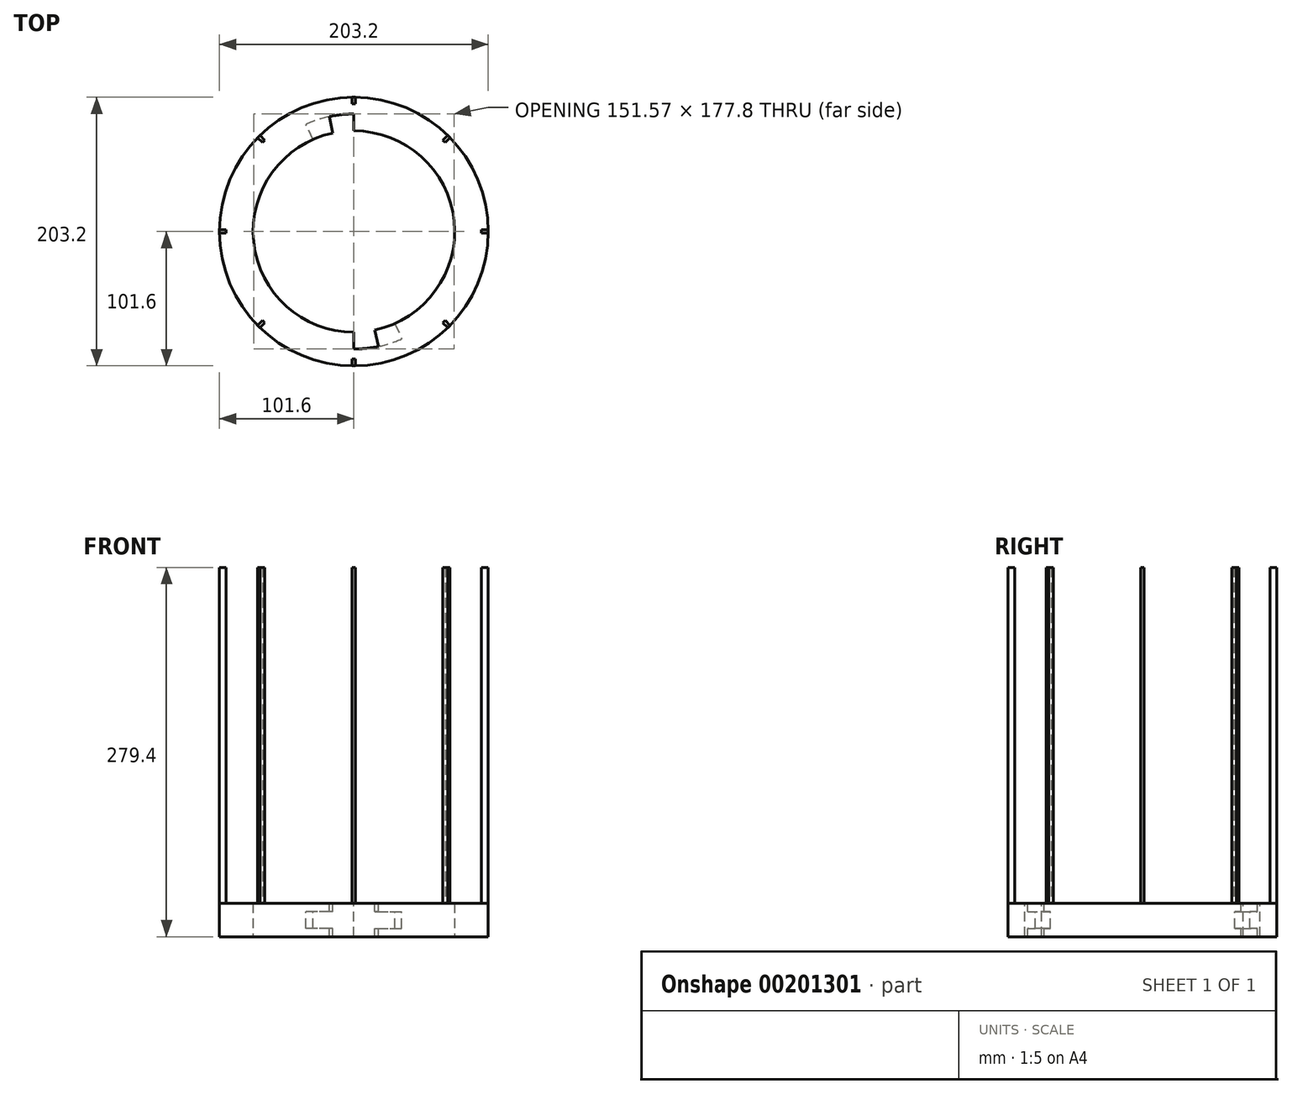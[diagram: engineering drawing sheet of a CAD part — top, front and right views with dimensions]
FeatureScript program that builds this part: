
annotation { "Feature Type Name" : "Feature", "Feature Type Description" : "" }
export const myFeature = defineFeature(function(context is Context, id is Id, definition is map)
    precondition{}
    {
        {
            var Q0;
            Q0=qCreatedBy(makeId("Top.planeOp"),FACE);
            var sketch = newSketch(context, id + "F0", { "sketchPlane" : qUnion([Q0])});
            skCircle(sketch, "E0", {"center": v(0, 0) * mm, "radius": 101.6 * mm});
            skCircle(sketch, "E1", {"center": v(0, 0) * mm, "radius": 76.2 * mm});
            skSolve(sketch);
        }
        {
            var Q0;
            Q0=makeQuery(id+"F0.imprint","IMPRINT",FACE,{"disambiguationData":[TD([[makeQuery(id+"F0.imprint","IMPRINT",EDGE,{"derivedFrom":sQuery(id+"F0.wireOp",EDGE,"E0")}),1.0]])]});
            extrude(context, id + "F1", {"entities" : qUnion([Q0]), "depth" : 25.4 * mm});
        }
        {
            var Q0;
            Q0=makeQuery(id+"F1.opExtrude","CAP_FACE",FACE,{"disambiguationData":[OSD([sQuery(id+"F0.wireOp",EDGE,"E0"),sQuery(id+"F0.wireOp",EDGE,"E1")])],"isStart":false});
            var sketch = newSketch(context, id + "F2", { "sketchPlane" : qUnion([Q0])});
            skLineSegment(sketch, "E2.bottom", {"start": v(1.27, 101.6) * mm, "end": v(-1.27, 101.6) * mm});
            skLineSegment(sketch, "E2.top", {"start": v(1.27, 96.51) * mm, "end": v(-1.27, 96.51) * mm});
            skLineSegment(sketch, "E2.left", {"start": v(1.27, 101.6) * mm, "end": v(1.27, 96.51) * mm});
            skLineSegment(sketch, "E2.right", {"start": v(-1.27, 101.6) * mm, "end": v(-1.27, 96.51) * mm});
            skPoint(sketch, "E2.middle", {"position": v(0, 99.05) * mm});
            skLineSegment(sketch, "E3", {"start": v(0, 0) * mm, "end": v(0, 101.6) * mm});
            skCircle(sketch, "E4", {"center": v(0, 0) * mm, "radius": 88.9 * mm});
            skLineSegment(sketch, "E5", {"start": v(0, 0) * mm, "end": v(-18.48, 86.96) * mm});
            skLineSegment(sketch, "E6", {"start": v(0, 0) * mm, "end": v(-36.16, 81.21) * mm});
            skLineSegment(sketch, "E7", {"start": v(0, 0) * mm, "end": v(0, -88.9) * mm});
            skLineSegment(sketch, "E8", {"start": v(0, 0) * mm, "end": v(18.48, -86.96) * mm});
            skLineSegment(sketch, "E9", {"start": v(0, 0) * mm, "end": v(36.16, -81.21) * mm});
            skSolve(sketch);
        }
        {
            var Q0;
            Q0=makeQuery(id+"F2.imprint","IMPRINT",FACE,{"disambiguationData":[TD([[makeQuery(id+"F2.imprint","IMPRINT",EDGE,{"derivedFrom":sQuery(id+"F2.wireOp",EDGE,"E2.bottom")}),1.0]])]});
            extrude(context, id + "F3", {"entities" : qUnion([Q0]), "depth" : 254 * mm});
        }
        {
            var Q0;
            Q0=qCreatedBy(makeId("Front.planeOp"),FACE);
            var sketch = newSketch(context, id + "F4", { "sketchPlane" : qUnion([Q0])});
            skLineSegment(sketch, "E10", {"start": v(0, 0) * mm, "end": v(0, 64.2) * mm});
            skSolve(sketch);
        }
        {
            var Q0;
            Q0=makeQuery(id+"F3.opExtrude","SWEPT_BODY",BODY,{"disambiguationData":[OSD([sQuery(id+"F2.wireOp",EDGE,"E2.bottom"),sQuery(id+"F2.wireOp",EDGE,"E2.top"),sQuery(id+"F2.wireOp",EDGE,"E2.left"),sQuery(id+"F2.wireOp",EDGE,"E2.right")])]});
            var Q1;
            Q1=sQuery(id+"F4.wireOp",EDGE,"E10");
            circularPattern(context, id + "F5", {"entities" : qUnion([Q0]), "axis" : qUnion([Q1]), "angle" : 360 * degree, "instanceCount" : 8, "equalSpace" : true});
        }
        {
            var Q0;
            {var subQ0=sQuery(id+"F2.wireOp",EDGE,"E4");var subQ1=sQuery(id+"F2.wireOp",EDGE,"E3");var subQ2=makeQuery(id+"F2.imprint","INTERSECT",VERTEX,{"derivedFrom":[subQ1,subQ0]});Q0=makeQuery(id+"F2.imprint","IMPRINT",FACE,{"disambiguationData":[TD([[makeQuery(id+"F2.imprint","IMPRINT",EDGE,{"disambiguationData":[TD([[subQ2,1.0]])],"derivedFrom":subQ1}),1.0]])]});}
            var Q1;
            {var subQ0=sQuery(id+"F2.wireOp",EDGE,"E7");var subQ1=sQuery(id+"F2.wireOp",EDGE,"E4");var subQ2=makeQuery(id+"F2.imprint","INTERSECT",VERTEX,{"derivedFrom":[subQ1,subQ0]});Q1=makeQuery(id+"F2.imprint","IMPRINT",FACE,{"disambiguationData":[TD([[makeQuery(id+"F2.imprint","IMPRINT",EDGE,{"disambiguationData":[TD([[subQ2,-1.0]])],"derivedFrom":subQ1}),1.0]])]});}
            extrude(context, id + "F6", {"entities" : qUnion([Q0, Q1]), "operationType" : NewBodyOperationType.REMOVE, "oppositeDirection" : true, "depth" : 25.4 * mm});
        }
        {
            var Q0;
            {var subQ0=sQuery(id+"F2.wireOp",EDGE,"E5");var subQ1=sQuery(id+"F2.wireOp",EDGE,"E4");var subQ2=makeQuery(id+"F2.imprint","INTERSECT",VERTEX,{"derivedFrom":[subQ1,subQ0]});Q0=makeQuery(id+"F2.imprint","IMPRINT",FACE,{"disambiguationData":[TD([[makeQuery(id+"F2.imprint","IMPRINT",EDGE,{"disambiguationData":[TD([[subQ2,-1.0]])],"derivedFrom":subQ1}),1.0]])]});}
            var Q1;
            {var subQ0=sQuery(id+"F2.wireOp",EDGE,"E8");var subQ1=sQuery(id+"F2.wireOp",EDGE,"E4");var subQ2=makeQuery(id+"F2.imprint","INTERSECT",VERTEX,{"derivedFrom":[subQ1,subQ0]});Q1=makeQuery(id+"F2.imprint","IMPRINT",FACE,{"disambiguationData":[TD([[makeQuery(id+"F2.imprint","IMPRINT",EDGE,{"disambiguationData":[TD([[subQ2,-1.0]])],"derivedFrom":subQ1}),1.0]])]});}
            extrude(context, id + "F7", {"entities" : qUnion([Q0, Q1]), "operationType" : NewBodyOperationType.REMOVE, "oppositeDirection" : true, "depth" : 19.05 * mm});
        }
        {
            var Q0;
            Q0=makeQuery(id+"F1.opExtrude","CAP_FACE",FACE,{"disambiguationData":[OSD([sQuery(id+"F0.wireOp",EDGE,"E0"),sQuery(id+"F0.wireOp",EDGE,"E1")])],"isStart":false});
            var sketch = newSketch(context, id + "F8", { "sketchPlane" : qUnion([Q0])});
            skLineSegment(sketch, "E11", {"start": v(18.48, -86.96) * mm, "end": v(-18.48, 86.96) * mm});
            skLineSegment(sketch, "E12", {"start": v(-36.16, 81.21) * mm, "end": v(36.16, -81.21) * mm});
            skCircle(sketch, "E13", {"center": v(0, 0) * mm, "radius": 76.2 * mm});
            skSolve(sketch);
        }
        {
            var Q0;
            {var subQ5=sQuery(id+"F8.wireOp",EDGE,"E13");var subQ7=sQuery(id+"F8.wireOp",EDGE,"E12");var subQ9=makeQuery(id+"F8.imprint","INTERSECT",VERTEX,{"disambiguationData":[OD(0.0)],"derivedFrom":[subQ7,subQ5]});Q0=makeQuery(id+"F8.imprint","IMPRINT",FACE,{"disambiguationData":[TD([[makeQuery(id+"F8.imprint","IMPRINT",EDGE,{"disambiguationData":[TD([[subQ9,1.0]])],"derivedFrom":subQ5}),-1.0]])]});}
            var Q1;
            {var subQ5=sQuery(id+"F8.wireOp",EDGE,"E13");var subQ7=sQuery(id+"F8.wireOp",EDGE,"E12");var subQ9=makeQuery(id+"F8.imprint","INTERSECT",VERTEX,{"disambiguationData":[OD(1.0)],"derivedFrom":[subQ7,subQ5]});Q1=makeQuery(id+"F8.imprint","IMPRINT",FACE,{"disambiguationData":[TD([[makeQuery(id+"F8.imprint","IMPRINT",EDGE,{"disambiguationData":[TD([[subQ9,1.0]])],"derivedFrom":subQ5}),-1.0]])]});}
            extrude(context, id + "F9", {"entities" : qUnion([Q0, Q1]), "operationType" : NewBodyOperationType.ADD, "oppositeDirection" : true, "depth" : 6.35 * mm});
        }
    });
